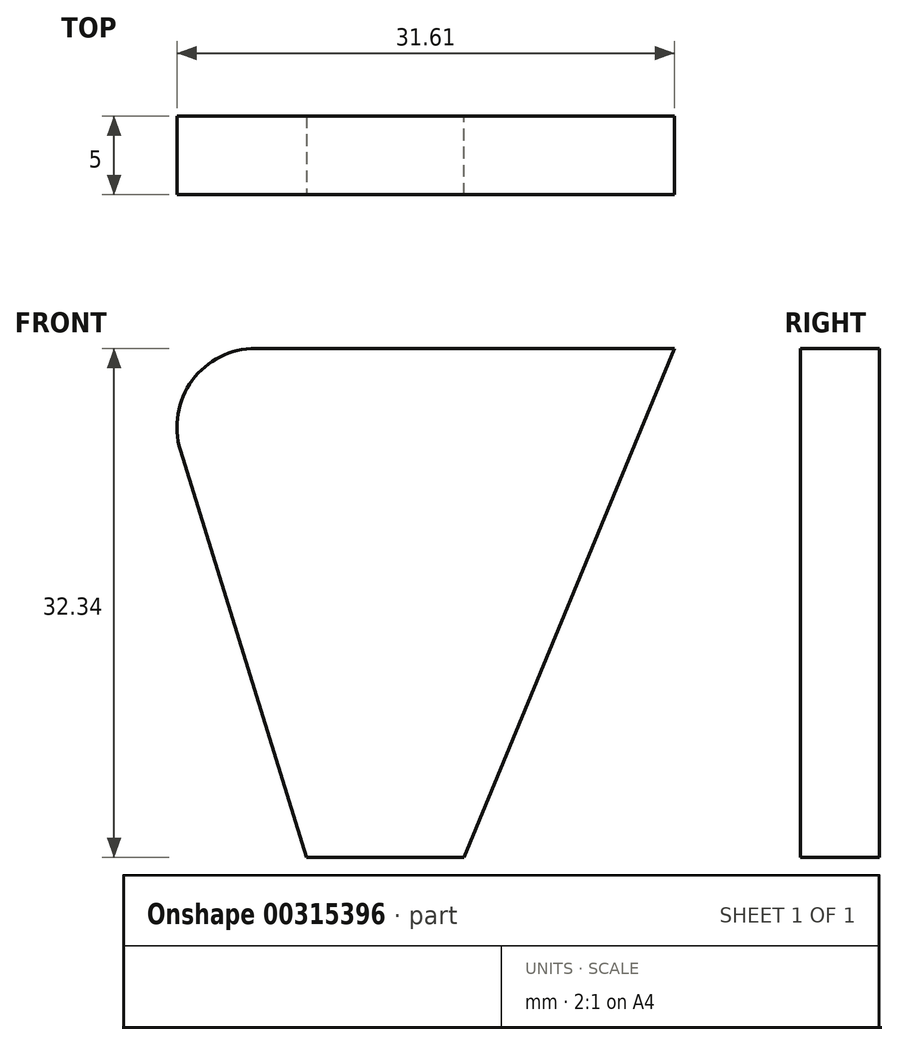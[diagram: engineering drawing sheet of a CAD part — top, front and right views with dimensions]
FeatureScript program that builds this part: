
annotation { "Feature Type Name" : "Feature", "Feature Type Description" : "" }
export const myFeature = defineFeature(function(context is Context, id is Id, definition is map)
    precondition{}
    {
        {
            var Q0;
            Q0=qCreatedBy(makeId("Front.planeOp"),FACE);
            var sketch = newSketch(context, id + "F0", { "sketchPlane" : qUnion([Q0])});
            skLineSegment(sketch, "E0.bottom", {"start": v(0, 0) * mm, "end": v(20, 0) * mm});
            skLineSegment(sketch, "E0.top", {"start": v(0, 32.34) * mm, "end": v(20, 32.34) * mm});
            skLineSegment(sketch, "E0.left", {"start": v(0, 0) * mm, "end": v(0, 32.34) * mm});
            skLineSegment(sketch, "E0.right", {"start": v(20, 0) * mm, "end": v(20, 32.34) * mm});
            skLineSegment(sketch, "E1", {"start": v(20, 0) * mm, "end": v(33.4, 32.34) * mm});
            skLineSegment(sketch, "E2", {"start": v(33.4, 32.34) * mm, "end": v(20, 32.34) * mm});
            skSolve(sketch);
        }
        {
            var Q0;
            Q0=makeQuery(id+"F0.imprint","IMPRINT",FACE,{"disambiguationData":[TD([[makeQuery(id+"F0.imprint","IMPRINT",EDGE,{"derivedFrom":sQuery(id+"F0.wireOp",EDGE,"E0.bottom")}),1.0]])]});
            var Q1;
            Q1=makeQuery(id+"F0.imprint","IMPRINT",FACE,{"disambiguationData":[TD([[makeQuery(id+"F0.imprint","IMPRINT",EDGE,{"derivedFrom":sQuery(id+"F0.wireOp",EDGE,"E0.right")}),-1.0]])]});
            extrude(context, id + "F1", {"entities" : qUnion([Q0, Q1]), "depth" : 5 * mm});
        }
        {
            var Q0;
            Q0=makeQuery(id+"F1.opExtrude","CAP_FACE",FACE,{"disambiguationData":[OSD([sQuery(id+"F0.wireOp",EDGE,"E0.bottom"),sQuery(id+"F0.wireOp",EDGE,"E0.top"),sQuery(id+"F0.wireOp",EDGE,"E0.left"),sQuery(id+"F0.wireOp",EDGE,"E1"),sQuery(id+"F0.wireOp",EDGE,"E2")])],"isStart":false});
            var sketch = newSketch(context, id + "F2", { "sketchPlane" : qUnion([Q0])});
            skLineSegment(sketch, "E3.0.0", {"start": v(33.4, 32.34) * mm, "end": v(0, 32.34) * mm});
            skLineSegment(sketch, "E3.0.1", {"start": v(0, 32.34) * mm, "end": v(0, 0) * mm});
            skLineSegment(sketch, "E3.0.2", {"start": v(0, 0) * mm, "end": v(20, 0) * mm});
            skLineSegment(sketch, "E3.0.3", {"start": v(20, 0) * mm, "end": v(33.4, 32.34) * mm});
            skLineSegment(sketch, "E4", {"start": v(0, 32.34) * mm, "end": v(10, 0) * mm});
            skSolve(sketch);
        }
        {
            var Q0;
            {var subQ0=sQuery(id+"F2.wireOp",EDGE,"E3.0.1");Q0=makeQuery(id+"F2.imprint","IMPRINT",FACE,{"disambiguationData":[TD([[makeQuery(id+"F2.imprint","IMPRINT",EDGE,{"derivedFrom":subQ0}),-1.0]])]});}
            extrude(context, id + "F3", {"entities" : qUnion([Q0]), "operationType" : NewBodyOperationType.REMOVE, "oppositeDirection" : true, "depth" : 25 * mm});
        }
        {
            var Q0;
            Q0=makeQuery(id+"F3.boolean.opBoolean","MERGE",EDGE,{"derivedFrom":[makeQuery(id+"F1.opExtrude","SWEPT_EDGE",EDGE,{"disambiguationData":[OSD([sQuery(id+"F0.wireOp",EDGE,"E0.top"),sQuery(id+"F0.wireOp",EDGE,"E0.left")])]}),makeQuery(id+"F3.opExtrude","SWEPT_EDGE",EDGE,{"disambiguationData":[OSD([sQuery(id+"F2.wireOp",EDGE,"E3.0.0"),sQuery(id+"F2.wireOp",EDGE,"E3.0.1"),sQuery(id+"F2.wireOp",EDGE,"E4")])]})]});
            fillet(context, id + "F4", {"entities" : qUnion([Q0]), "radius" : 5 * mm, "tangentPropagation" : true, "allowEdgeOverflow" : false});
        }
    });
